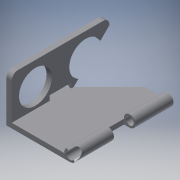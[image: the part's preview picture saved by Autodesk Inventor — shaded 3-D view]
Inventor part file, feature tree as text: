
AUTODESK INVENTOR PART (.ipt)
format: ipt  version: 2016 (Build 200138000, 138)  size: 317,440 bytes
history: native  units: in
note: dims shown in document units (in); Inventor stores cm internally (conversion verified against a paired STEP export)
features: extrude x19, sketch x19, projected_geometry x6, reference x3, fillet x2, plane x1
ambient origin geometry x8: Origin, YZ Plane, XZ Plane, XY Plane, X Axis, Y Axis, Z Axis, Center Point
bodies: Solid1 (feature_tree)
feature tree (50):
  extrude  "Extrusion1"  Depth=0.05in
  plane  "Work Plane1"
  extrude  "Extrusion2"  Depth=0.1496in
  extrude  "Extrusion3"  [1 undecoded]
  sketch  "Sketch4"  dims[d7=0.4in d8=0.0in d9=1.1in]
  extrude  "Extrusion4"  Depth=1.1in
  extrude  "Extrusion5"  Depth=1.1in
  extrude  "Extrusion6"  Depth=1.05in
  extrude  "Extrusion7"  Depth=1.05in
  extrude  "Extrusion8"  Depth=1.2in
  extrude  "Extrusion9"  Depth=1.2in
  extrude  "Extrusion10"  Depth=1.1in
  fillet  "Fillet1"  Radius=1.1in
  extrude  "Extrusion12"  Depth=1.0in TaperAngle=0.0deg
  extrude  "Extrusion13"  Depth=0.05in TaperAngle=0.0deg
  extrude  "Extrusion14"  Depth=0.8661in TaperAngle=0.0deg
  extrude  "Extrusion15"  Depth=0.3937in TaperAngle=0.0deg
  extrude  "Extrusion16"  Depth=0.125in TaperAngle=0.0deg
  extrude  "Extrusion17"  Depth=0.5906in TaperAngle=0.0deg
  extrude  "Extrusion18"  Depth=0.6693in
  extrude  "Extrusion19"  Depth=1.0in TaperAngle=0.0deg
  extrude  "Extrusion20"  Depth=0.0098in TaperAngle=0.0deg
  fillet  "Fillet2"  Radius=0.08in
  sketch  "Sketch1"  dims[d0=0.15in d1=0.05in]
  sketch  "Sketch2"  dims[d2=0.2362in d3=0.1496in]
  sketch  "Sketch3"  dims[d4=1.2in d5=0.0in d6=-0.4in]
  sketch  "Sketch5"  dims[d10=1.1in d11=1.1in]
  sketch  "Sketch6"  dims[d12=0.05in d13=1.05in]
  sketch  "Sketch7"  dims[d14=0.05in d15=1.05in]
  sketch  "Sketch8"  dims[d16=1.0in d17=0.0in d18=1.2in]
  reference  "Reference1"
  sketch  "Sketch9"  dims[d19=1.2in d20=1.2in]
  projected_geometry  "Projected Loop1"
  sketch  "Sketch10"  dims[d21=1.1in d22=1.1in d23=1.1in]
  projected_geometry  "Projected Loop2"
  sketch  "Sketch12"  dims[d24=1.0in d25=0.0in d26=1.0in d27=0.0in]
  projected_geometry  "Projected Loop3"
  sketch  "Sketch13"  dims[d28=0.05in d29=0.0in d30=0.05in d31=0.0in]
  sketch  "Sketch14"  dims[d32=0.1083in d35=0.8661in d36=0.0in]
  projected_geometry  "Projected Loop4"
  sketch  "Sketch15"  dims[d37=0.3937in d38=0.0in d39=0.3937in d40=0.0in]
  sketch  "Sketch16"  dims[d45=0.125in d46=0.4724in d47=0.0in]
  reference  "Reference4"
  reference  "Reference5"
  sketch  "Sketch17"  dims[d48=199.0in d49=0.0in d50=0.5906in d51=0.0in]
  projected_geometry  "Projected Loop5"
  sketch  "Sketch18"  dims[d52=0.5906in d53=0.0in d54=0.6693in]
  projected_geometry  "Projected Loop6"
  sketch  "Sketch19"  dims[d55=0.6693in d56=1.0in d57=0.0in]
  sketch  "Sketch20"  dims[d58=0.0197in d59=0.0in d60=0.0197in d61=0.0in d62=0.08in d63=0.0in d64=0.22in d65=0.44in d66=0.1in d67=1.0in d68=0.0in d69=0.0098in]
note: 1 required parameter value undecoded (feature->parameter linkage not recoverable at this tier; creation-order binding heuristic only, values carry confidence <= 0.55)
